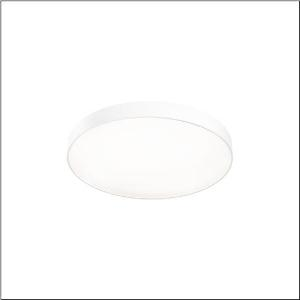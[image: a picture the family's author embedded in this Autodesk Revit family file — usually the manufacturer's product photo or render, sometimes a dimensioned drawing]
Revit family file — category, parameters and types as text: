
# Revit family: round_21_m_51mr36gd0421w
name_source: partatom
category: Lighting Fixtures
units: mm (PartAtom-declared; Revit-internal decimal feet)

## family parameters
Cut with Voids When Loaded = No
Host = Face
Light Source = No
Part Type = Normal
Room Calculation Point = No
Round Connector Dimension = Use Diameter
Shared = No

## types (1)
- Round 21 M (1 x LED, 7160 lm, 54.5 W, 4000K)
    Apparent Load = 55 VA
    CIE Flux Codes = 49 80 96 85 100
    Color Rendering = 80
    Color Temperature = 4000K
    Default Elevation = 1800 mm
    Description = Round 21 M, wall and ceiling luminaire, primary optical cover: cover, of PMMA, opal, light emission: direct/indirect distribution, primary light characteristic: symmetric, installation type: suspended mounting, surface-mounted, LED, rated luminous flux: 7.110lm, luminous efficacy: 130lm/W, light colour: 840, colour temperature: 4000K, with terminal, 5-pole, mains connection: 230V, AC, 50/60Hz, rated input power: 55W, housing, of aluminium, coated, white, diameter: 600mm, height: 62mm, protection rating (complete): IP40, insulation class (complete): insulation class I (protective earthing), certification: CE, impact resistance: IK04, permissible operating ambient temperature: -10..+35°C, packaging unit: 1 piece
    Height = 87 mm
    Lamp = 1 x LED
    Lamp Light Flux = 7160 lm
    Lamp Power = 54.5 W
    Lamp count = 1
    Length = 600 mm
    Luminous efficacy = 131 lm/W
    Manufacturer = Siteco
    ModVariant = No
    Model = 51MR36GD0421W
    Mounting Place = Ceiling
    Mounting Type = Surface mounted
    Number of Poles = 1
    OnlyDefault = Yes
    Power Factor = 1
    Product Name = Round 21 M
    Product group = wall and ceiling luminaire
    ProductGroupID = 301
    Protection Class = Protection class I
    Protection Degree = IP 40
    RLX_Detail_Level = 1
    RLX_Emergency_Light_Flux = 0 lm
    RLX_Emergency_Type = 0
    RLX_Emergency_Type_DB = No
    RlxData = <blob elided: 12085 chars, md5=be3db213>
    Socket = socket
    Standby Power = 0 W
    System Light Flux = 7160 lm
    System Power = 55 W
    Type Comments = Product without accessories
    Type Image = l_1258330.jpg
    URL = http://relux.com
    VarID = ---
    Voltage = 0 V
    Weight = 0.00 kg
    Width = 0 mm  [stored 0 ft]

note: [stored X ft] marks values corroborated as IEEE doubles in the binary element streams (Revit-internal decimal feet)

## geometry (parser evidence)
native form markers: Sweep x14
no freeform markers — native parametric forms only
